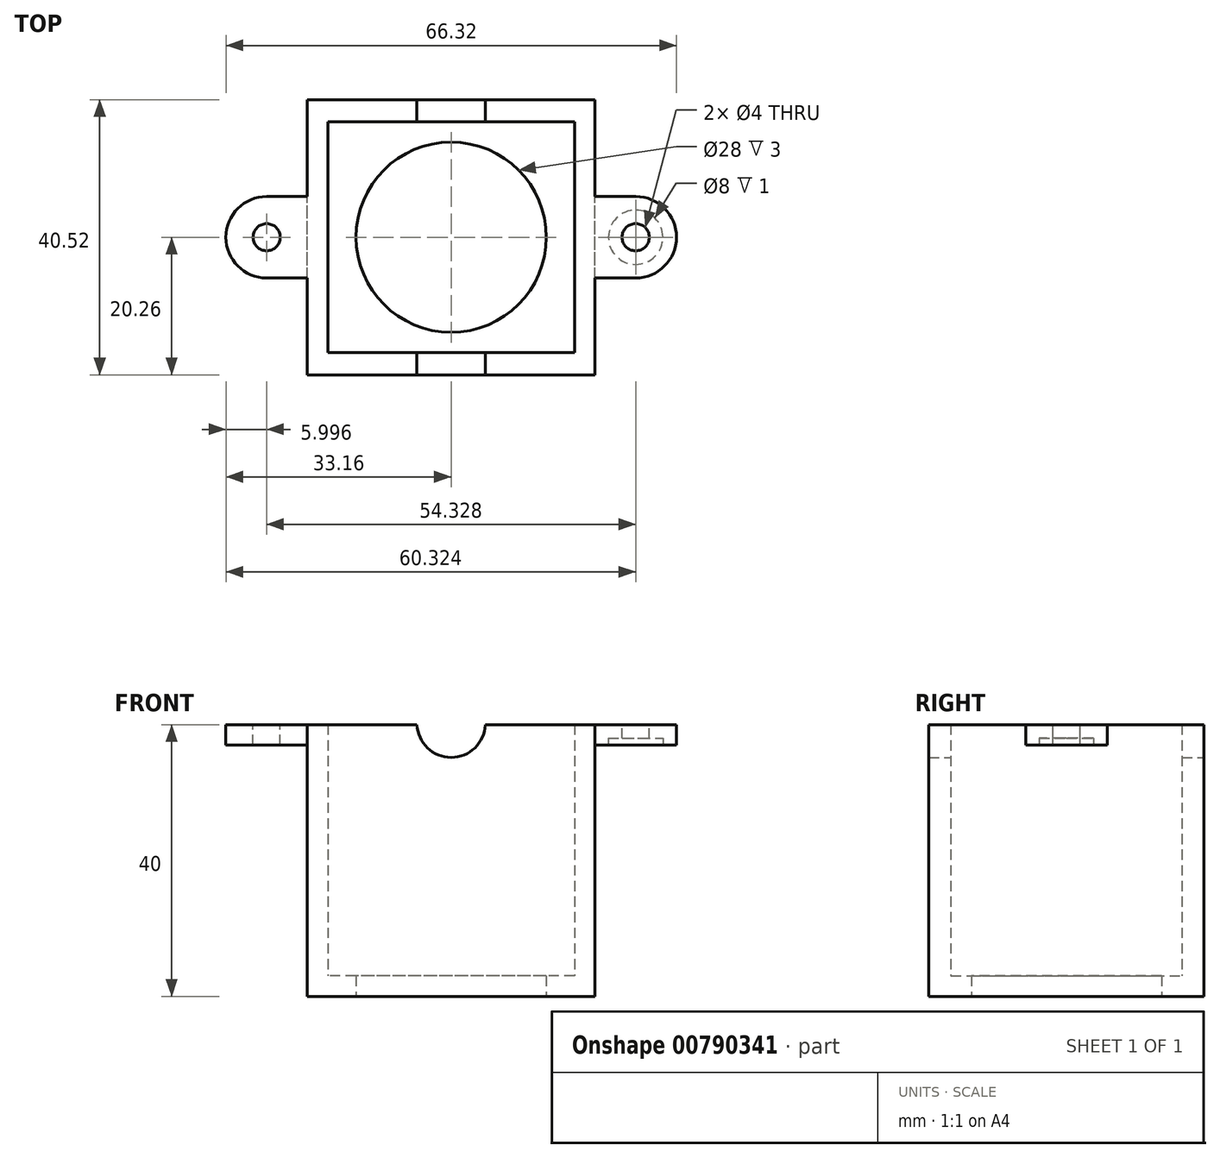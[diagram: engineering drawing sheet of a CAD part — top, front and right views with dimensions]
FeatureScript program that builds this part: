
annotation { "Feature Type Name" : "Feature", "Feature Type Description" : "" }
export const myFeature = defineFeature(function(context is Context, id is Id, definition is map)
    precondition{}
    {
        {
            var Q0;
            Q0=qCreatedBy(makeId("Top.planeOp"),FACE);
            var sketch = newSketch(context, id + "F0", { "sketchPlane" : qUnion([Q0])});
            skCircle(sketch, "E0", {"center": v(0, 0) * mm, "radius": 14 * mm});
            skLineSegment(sketch, "E1.bottom", {"start": v(18.16, -17) * mm, "end": v(-18.16, -17) * mm});
            skLineSegment(sketch, "E1.top", {"start": v(18.16, 17) * mm, "end": v(-18.16, 17) * mm});
            skLineSegment(sketch, "E1.left", {"start": v(18.16, -17) * mm, "end": v(18.16, 17) * mm});
            skLineSegment(sketch, "E1.right", {"start": v(-18.16, -17) * mm, "end": v(-18.16, 17) * mm});
            skLineSegment(sketch, "E2.bottom", {"start": v(21.16, -20.26) * mm, "end": v(-21.16, -20.26) * mm});
            skLineSegment(sketch, "E2.top", {"start": v(21.16, 20.26) * mm, "end": v(-21.16, 20.26) * mm});
            skLineSegment(sketch, "E2.left", {"start": v(21.16, -20.26) * mm, "end": v(21.16, 20.26) * mm});
            skLineSegment(sketch, "E2.right", {"start": v(-21.16, -20.26) * mm, "end": v(-21.16, 20.26) * mm});
            skSolve(sketch);
        }
        {
            var Q0;
            Q0=makeQuery(id+"F0.imprint","IMPRINT",FACE,{"disambiguationData":[TD([[makeQuery(id+"F0.imprint","IMPRINT",EDGE,{"derivedFrom":sQuery(id+"F0.wireOp",EDGE,"E0")}),-1.0]])]});
            extrude(context, id + "F1", {"entities" : qUnion([Q0]), "depth" : 3 * mm, "offsetDistance" : 25 * mm});
        }
        {
            var Q0;
            Q0 = qSketchRegion(id + "F0", true);
            extrude(context, id + "F2", {"entities" : qUnion([Q0]), "operationType" : NewBodyOperationType.ADD, "depth" : 40 * mm, "offsetDistance" : 25 * mm});
        }
        {
            var Q0;
            Q0=makeQuery(id+"F2.opExtrude","CAP_FACE",FACE,{"disambiguationData":[OSD([sQuery(id+"F0.wireOp",EDGE,"E1.bottom"),sQuery(id+"F0.wireOp",EDGE,"E1.top"),sQuery(id+"F0.wireOp",EDGE,"E1.left"),sQuery(id+"F0.wireOp",EDGE,"E1.right"),sQuery(id+"F0.wireOp",EDGE,"E2.bottom"),sQuery(id+"F0.wireOp",EDGE,"E2.top"),sQuery(id+"F0.wireOp",EDGE,"E2.left"),sQuery(id+"F0.wireOp",EDGE,"E2.right")])],"isStart":false});
            cPlane(context, id + "F3", {"entities" : qUnion([Q0]), "cplaneType" : CPlaneType.OFFSET, "offset" : 0 * mm, "width" : 150 * mm, "height" : 150 * mm});
        }
        {
            var Q0;
            Q0=qCreatedBy(id+"F3.planeOp",FACE);
            var sketch = newSketch(context, id + "F4", { "sketchPlane" : qUnion([Q0])});
            skLineSegment(sketch, "E3.0", {"start": v(-21.16, -20.26) * mm, "end": v(-21.16, 20.26) * mm});
            skLineSegment(sketch, "E4.0", {"start": v(21.16, 20.26) * mm, "end": v(-21.16, 20.26) * mm});
            skLineSegment(sketch, "E5.0", {"start": v(21.16, -20.26) * mm, "end": v(21.16, 20.26) * mm});
            skLineSegment(sketch, "E6.0", {"start": v(21.16, -20.26) * mm, "end": v(-21.16, -20.26) * mm});
            skLineSegment(sketch, "E7", {"start": v(-30.07, 0) * mm, "end": v(35.62, 0) * mm, "construction": true});
            skCircle(sketch, "E8", {"center": v(-27.16, 0) * mm, "radius": 6 * mm});
            skCircle(sketch, "E9", {"center": v(-27.16, 0) * mm, "radius": 4 * mm});
            skCircle(sketch, "E10", {"center": v(-27.16, 0) * mm, "radius": 2 * mm});
            skLineSegment(sketch, "E11", {"start": v(-27.16, 0) * mm, "end": v(-27.16, 9.85) * mm, "construction": true});
            skLineSegment(sketch, "E12", {"start": v(-27.16, 0) * mm, "end": v(-27.16, -9.92) * mm, "construction": true});
            skLineSegment(sketch, "E13", {"start": v(-27.16, 6) * mm, "end": v(-21.16, 6) * mm});
            skPoint(sketch, "E13.startSnap0", {"position": v(-27.16, 4.93) * mm});
            skLineSegment(sketch, "E14", {"start": v(-27.16, -6) * mm, "end": v(-21.16, -6) * mm});
            skLineSegment(sketch, "E15", {"start": v(0, 28.06) * mm, "end": v(0, -33.97) * mm, "construction": true});
            skLineSegment(sketch, "E16.MirrorCS", {"start": v(27.16, 6) * mm, "end": v(21.16, 6) * mm});
            skLineSegment(sketch, "E17.MirrorCS", {"start": v(27.16, -6) * mm, "end": v(21.16, -6) * mm});
            skCircle(sketch, "E18.MirrorC", {"center": v(27.16, 0) * mm, "radius": 6 * mm});
            skCircle(sketch, "E19.MirrorC", {"center": v(27.16, 0) * mm, "radius": 4 * mm});
            skCircle(sketch, "E20.MirrorC", {"center": v(27.16, 0) * mm, "radius": 2 * mm});
            skSolve(sketch);
        }
        {
            var Q0;
            Q0=makeQuery(id+"F4.imprint","IMPRINT",FACE,{"disambiguationData":[TD([[makeQuery(id+"F4.imprint","IMPRINT",EDGE,{"derivedFrom":sQuery(id+"F4.wireOp",EDGE,"E9")}),-1.0]])]});
            var Q1;
            {var subQ0=sQuery(id+"F4.wireOp",EDGE,"E13");Q1=makeQuery(id+"F4.imprint","IMPRINT",FACE,{"disambiguationData":[TD([[makeQuery(id+"F4.imprint","IMPRINT",EDGE,{"derivedFrom":subQ0}),-1.0]])]});}
            var Q2;
            Q2=makeQuery(id+"F4.imprint","IMPRINT",FACE,{"disambiguationData":[TD([[makeQuery(id+"F4.imprint","IMPRINT",EDGE,{"derivedFrom":sQuery(id+"F4.wireOp",EDGE,"E9")}),1.0]])]});
            var Q3;
            {var subQ0=sQuery(id+"F4.wireOp",EDGE,"E16.MirrorCS");Q3=makeQuery(id+"F4.imprint","IMPRINT",FACE,{"disambiguationData":[TD([[makeQuery(id+"F4.imprint","IMPRINT",EDGE,{"derivedFrom":subQ0}),1.0]])]});}
            var Q4;
            Q4=makeQuery(id+"F4.imprint","IMPRINT",FACE,{"disambiguationData":[TD([[makeQuery(id+"F4.imprint","IMPRINT",EDGE,{"derivedFrom":sQuery(id+"F4.wireOp",EDGE,"E19.MirrorC")}),1.0]])]});
            var Q5;
            Q5=makeQuery(id+"F4.imprint","IMPRINT",FACE,{"disambiguationData":[TD([[makeQuery(id+"F4.imprint","IMPRINT",EDGE,{"derivedFrom":sQuery(id+"F4.wireOp",EDGE,"E19.MirrorC")}),-1.0]])]});
            extrude(context, id + "F5", {"entities" : qUnion([Q0, Q1, Q2, Q3, Q4, Q5]), "operationType" : NewBodyOperationType.ADD, "depth" : -3 * mm, "offsetDistance" : 25 * mm});
        }
        {
            var Q0;
            Q0=makeQuery(id+"F2.opExtrude","SWEPT_FACE",FACE,{"disambiguationData":[OSD([sQuery(id+"F0.wireOp",EDGE,"E2.top")])]});
            cPlane(context, id + "F6", {"entities" : qUnion([Q0]), "cplaneType" : CPlaneType.OFFSET, "offset" : 0 * mm, "width" : 150 * mm, "height" : 150 * mm});
        }
        {
            var Q0;
            Q0=qCreatedBy(id+"F6.planeOp",FACE);
            var sketch = newSketch(context, id + "F7", { "sketchPlane" : qUnion([Q0])});
            skLineSegment(sketch, "E21", {"start": v(-9.6, 40.22) * mm, "end": v(9.27, 40.22) * mm});
            skCircle(sketch, "E22", {"center": v(0, 40.22) * mm, "radius": 5.04 * mm});
            skSolve(sketch);
        }
        {
            var Q0;
            {var subQ0=sQuery(id+"F7.wireOp",EDGE,"E22");var subQ1=sQuery(id+"F7.wireOp",EDGE,"E21");var subQ2=makeQuery(id+"F7.imprint","INTERSECT",VERTEX,{"disambiguationData":[OD(0.0)],"derivedFrom":[subQ1,subQ0]});Q0=makeQuery(id+"F7.imprint","IMPRINT",FACE,{"disambiguationData":[TD([[makeQuery(id+"F7.imprint","IMPRINT",EDGE,{"disambiguationData":[TD([[subQ2,1.0]])],"derivedFrom":subQ1}),-1.0]])]});}
            extrude(context, id + "F8", {"entities" : qUnion([Q0]), "operationType" : NewBodyOperationType.REMOVE, "oppositeDirection" : true, "depth" : 100 * mm, "offsetDistance" : 25 * mm});
        }
        {
            var Q0;
            Q0=makeQuery(id+"F5.opExtrude","CAP_FACE",FACE,{"disambiguationData":[OSD([sQuery(id+"F4.wireOp",EDGE,"E5.0"),sQuery(id+"F4.wireOp",EDGE,"E16.MirrorCS"),sQuery(id+"F4.wireOp",EDGE,"E17.MirrorCS"),sQuery(id+"F4.wireOp",EDGE,"E18.MirrorC"),sQuery(id+"F4.wireOp",EDGE,"E20.MirrorC")])],"isStart":false});
            cPlane(context, id + "F9", {"entities" : qUnion([Q0]), "cplaneType" : CPlaneType.OFFSET, "offset" : 0 * mm, "width" : 150 * mm, "height" : 150 * mm});
        }
        {
            var Q0;
            Q0=qCreatedBy(id+"F9.planeOp",FACE);
            var sketch = newSketch(context, id + "F10", { "sketchPlane" : qUnion([Q0])});
            skCircle(sketch, "E23.0", {"center": v(27.16, 0) * mm, "radius": 4 * mm});
            skCircle(sketch, "E24.0", {"center": v(-27.16, 0) * mm, "radius": 4 * mm});
            skSolve(sketch);
        }
        {
            var Q0;
            Q0=makeQuery(id+"F10.imprint","IMPRINT",FACE,{"disambiguationData":[TD([[makeQuery(id+"F10.imprint","IMPRINT",EDGE,{"derivedFrom":sQuery(id+"F10.wireOp",EDGE,"E23.0")}),1.0]])]});
            var Q1;
            Q1=makeQuery(id+"F10.imprint","IMPRINT",FACE,{"disambiguationData":[TD([[makeQuery(id+"F10.imprint","IMPRINT",EDGE,{"derivedFrom":sQuery(id+"F10.wireOp",EDGE,"E24.0")}),-1.0]])]});
            extrude(context, id + "F11", {"entities" : qUnion([Q0, Q1]), "operationType" : NewBodyOperationType.REMOVE, "oppositeDirection" : true, "depth" : 1 * mm, "offsetDistance" : 25 * mm});
        }
    });
